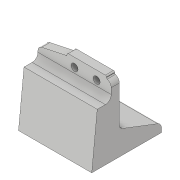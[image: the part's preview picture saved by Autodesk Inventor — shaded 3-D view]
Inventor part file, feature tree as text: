
AUTODESK INVENTOR PART (.ipt)
format: ipt  version: 2018 (Build 220112000, 112)  size: 146,944 bytes
history: native  units: in
note: dims shown in document units (in); Inventor stores cm internally (conversion verified against a paired STEP export)
features: fillet x4, sketch x4, extrude x3, hole x1
ambient origin geometry x8: Origin, YZ Plane, XZ Plane, XY Plane, X Axis, Y Axis, Z Axis, Center Point
bodies: Solid1 (feature_tree)
feature tree (12):
  extrude  "Extrusion1"  Depth=1.2in
  extrude  "Extrusion2"  Depth=1.2in
  extrude  "Extrusion3"  Depth=0.14in
  fillet  "Fillet1"  Radius=0.38in
  fillet  "Fillet2"  Radius=0.14in
  fillet  "Fillet3"  Radius=1.26in
  fillet  "Fillet4"  Radius=0.0825in
  hole  "Hole2"  [1 undecoded]
  sketch  "Sketch2"  dims[d0=1.2in d1=0.1443in]
  sketch  "Sketch3"  dims[d2=0.5772in d3=1.2in]
  sketch  "Sketch4"  dims[d4=0.9in d5=0.14in d6=0.38in d7=0.14in d8=1.26in d9=0.0in d10=0.0825in]
  sketch  "Sketch5"  dims[d11=0.5in d12=1.26in d13=0.0in d15=0.04in d16=1.26in d17=0.0in d18=0.68in d28=0.38in d29=0.19in d30=0.25in d31=0.12in d32=0.75in d33=0.375in d34=0.25in d35=0.5635in d36=1.0in d37=0.8108in d38=0.1in d39=0.08in d40=0.1in d41=0.08in d42=0.1in d43=0.02in]
note: 1 required parameter value undecoded (feature->parameter linkage not recoverable at this tier; creation-order binding heuristic only, values carry confidence <= 0.55)
